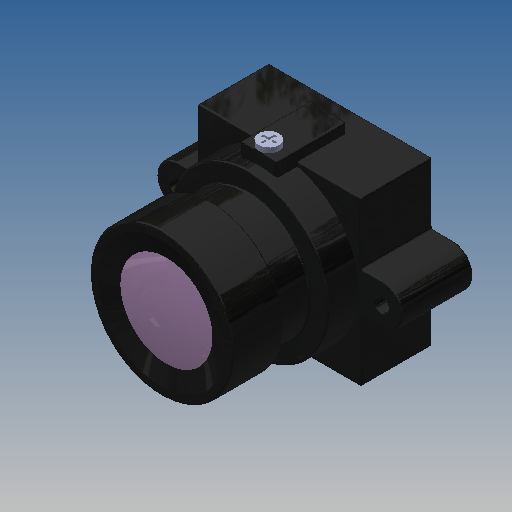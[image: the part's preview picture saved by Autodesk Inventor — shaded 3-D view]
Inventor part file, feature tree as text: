
AUTODESK INVENTOR PART (.ipt)
format: ipt  version: 2020 (Build 240168000, 168)  size: 301,056 bytes
history: native  units: mm
features: other x1, fillet x1
ambient origin geometry x8: Origin, YZ Plane, XZ Plane, XY Plane, X Axis, Y Axis, Z Axis, Center Point
bodies: Body1 (feature_tree)
feature tree (2):
  other  "Твердое тело1"
  fillet  "Fillet3"  [1 undecoded]
note: 1 required parameter value undecoded (feature->parameter linkage not recoverable at this tier; creation-order binding heuristic only, values carry confidence <= 0.55)
